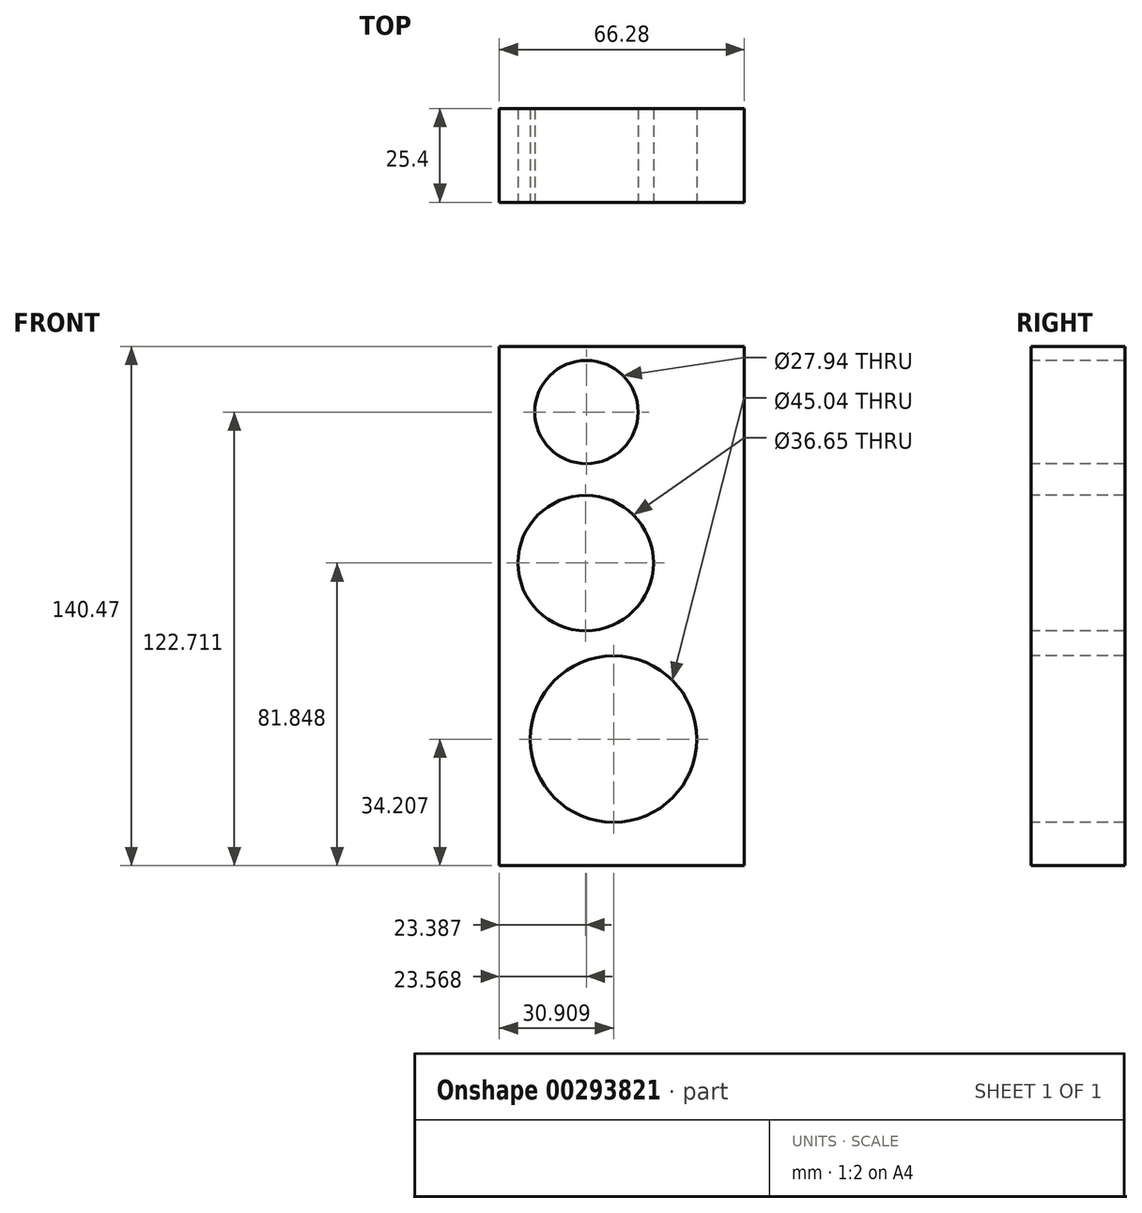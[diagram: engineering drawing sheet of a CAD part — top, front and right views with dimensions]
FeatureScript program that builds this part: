
annotation { "Feature Type Name" : "Feature", "Feature Type Description" : "" }
export const myFeature = defineFeature(function(context is Context, id is Id, definition is map)
    precondition{}
    {
        {
            var Q0;
            Q0=qCreatedBy(makeId("Front.planeOp"),FACE);
            var sketch = newSketch(context, id + "F0", { "sketchPlane" : qUnion([Q0])});
            skLineSegment(sketch, "E0.bottom", {"start": v(-53.09, 57.22) * mm, "end": v(13.2, 57.22) * mm});
            skLineSegment(sketch, "E0.top", {"start": v(-53.09, -83.25) * mm, "end": v(13.2, -83.25) * mm});
            skLineSegment(sketch, "E0.left", {"start": v(-53.09, 57.22) * mm, "end": v(-53.09, -83.25) * mm});
            skLineSegment(sketch, "E0.right", {"start": v(13.2, 57.22) * mm, "end": v(13.2, -83.25) * mm});
            skSolve(sketch);
        }
        {
            var Q0;
            Q0=makeQuery(id+"F0.imprint","IMPRINT",FACE,{"disambiguationData":[TD([[makeQuery(id+"F0.imprint","IMPRINT",EDGE,{"derivedFrom":sQuery(id+"F0.wireOp",EDGE,"E0.bottom")}),-1.0]])]});
            extrude(context, id + "F1", {"entities" : qUnion([Q0]), "depth" : 25.4 * mm});
        }
        {
            var Q0;
            Q0=makeQuery(id+"F1.opExtrude","CAP_FACE",FACE,{"disambiguationData":[OSD([sQuery(id+"F0.wireOp",EDGE,"E0.bottom"),sQuery(id+"F0.wireOp",EDGE,"E0.top"),sQuery(id+"F0.wireOp",EDGE,"E0.left"),sQuery(id+"F0.wireOp",EDGE,"E0.right")])],"isStart":false});
            var sketch = newSketch(context, id + "F2", { "sketchPlane" : qUnion([Q0])});
            skCircle(sketch, "E1", {"center": v(-29.52, 39.46) * mm, "radius": 13.97 * mm});
            skCircle(sketch, "E2", {"center": v(-24.25, -4.2) * mm, "radius": 21.63 * mm});
            skCircle(sketch, "E3", {"center": v(-30.18, -45.8) * mm, "radius": 23.7 * mm});
            skSolve(sketch);
        }
        {
            var Q0;
            Q0=makeQuery(id+"F2.imprint","IMPRINT",FACE,{"disambiguationData":[TD([[makeQuery(id+"F2.imprint","IMPRINT",EDGE,{"derivedFrom":sQuery(id+"F2.wireOp",EDGE,"E1")}),1.0]])]});
            extrude(context, id + "F3", {"entities" : qUnion([Q0]), "operationType" : NewBodyOperationType.REMOVE, "oppositeDirection" : true, "depth" : 25.4 * mm});
        }
        {
            var Q0;
            Q0=makeQuery(id+"F1.opExtrude","CAP_FACE",FACE,{"disambiguationData":[OSD([sQuery(id+"F0.wireOp",EDGE,"E0.bottom"),sQuery(id+"F0.wireOp",EDGE,"E0.top"),sQuery(id+"F0.wireOp",EDGE,"E0.left"),sQuery(id+"F0.wireOp",EDGE,"E0.right")])],"isStart":false});
            var sketch = newSketch(context, id + "F4", { "sketchPlane" : qUnion([Q0])});
            skCircle(sketch, "E4", {"center": v(-25.56, -7.87) * mm, "radius": 19.03 * mm});
            skSolve(sketch);
        }
        {
            var Q0;
            Q0=makeQuery(id+"F4.imprint","IMPRINT",FACE,{"disambiguationData":[TD([[makeQuery(id+"F4.imprint","IMPRINT",EDGE,{"derivedFrom":sQuery(id+"F4.wireOp",EDGE,"E4")}),1.0]])]});
            extrude(context, id + "F5", {"entities" : qUnion([Q0]), "operationType" : NewBodyOperationType.ADD, "depth" : 25.4 * mm});
        }
        {
            var Q0;
            Q0=makeQuery(id+"F5.opExtrude","CAP_FACE",FACE,{"disambiguationData":[OSD([sQuery(id+"F4.wireOp",EDGE,"E4")])],"isStart":false});
            extrude(context, id + "F6", {"entities" : qUnion([Q0]), "operationType" : NewBodyOperationType.REMOVE, "oppositeDirection" : true, "depth" : 25.4 * mm});
        }
        {
            var Q0;
            Q0=makeQuery(id+"F6.boolean.opBoolean","MERGE",FACE,{"derivedFrom":[makeQuery(id+"F1.opExtrude","CAP_FACE",FACE,{"disambiguationData":[OSD([sQuery(id+"F0.wireOp",EDGE,"E0.bottom"),sQuery(id+"F0.wireOp",EDGE,"E0.top"),sQuery(id+"F0.wireOp",EDGE,"E0.left"),sQuery(id+"F0.wireOp",EDGE,"E0.right")])],"isStart":false}),makeQuery(id+"F6.opExtrude","CAP_FACE",FACE,{"disambiguationData":[OSD([sQuery(id+"F4.wireOp",EDGE,"E4")])],"isStart":false})]});
            var sketch = newSketch(context, id + "F7", { "sketchPlane" : qUnion([Q0])});
            skCircle(sketch, "E5", {"center": v(-29.7, -1.4) * mm, "radius": 18.32 * mm});
            skCircle(sketch, "E6", {"center": v(-22.18, -49.04) * mm, "radius": 22.52 * mm});
            skSolve(sketch);
        }
        {
            var Q0;
            Q0=makeQuery(id+"F7.imprint","IMPRINT",FACE,{"disambiguationData":[TD([[makeQuery(id+"F7.imprint","IMPRINT",EDGE,{"derivedFrom":sQuery(id+"F7.wireOp",EDGE,"E5")}),1.0]])]});
            var Q1;
            Q1=makeQuery(id+"F7.imprint","IMPRINT",FACE,{"disambiguationData":[TD([[makeQuery(id+"F7.imprint","IMPRINT",EDGE,{"derivedFrom":sQuery(id+"F7.wireOp",EDGE,"E6")}),1.0]])]});
            extrude(context, id + "F8", {"entities" : qUnion([Q0, Q1]), "operationType" : NewBodyOperationType.REMOVE, "oppositeDirection" : true, "depth" : 25.4 * mm});
        }
    });
